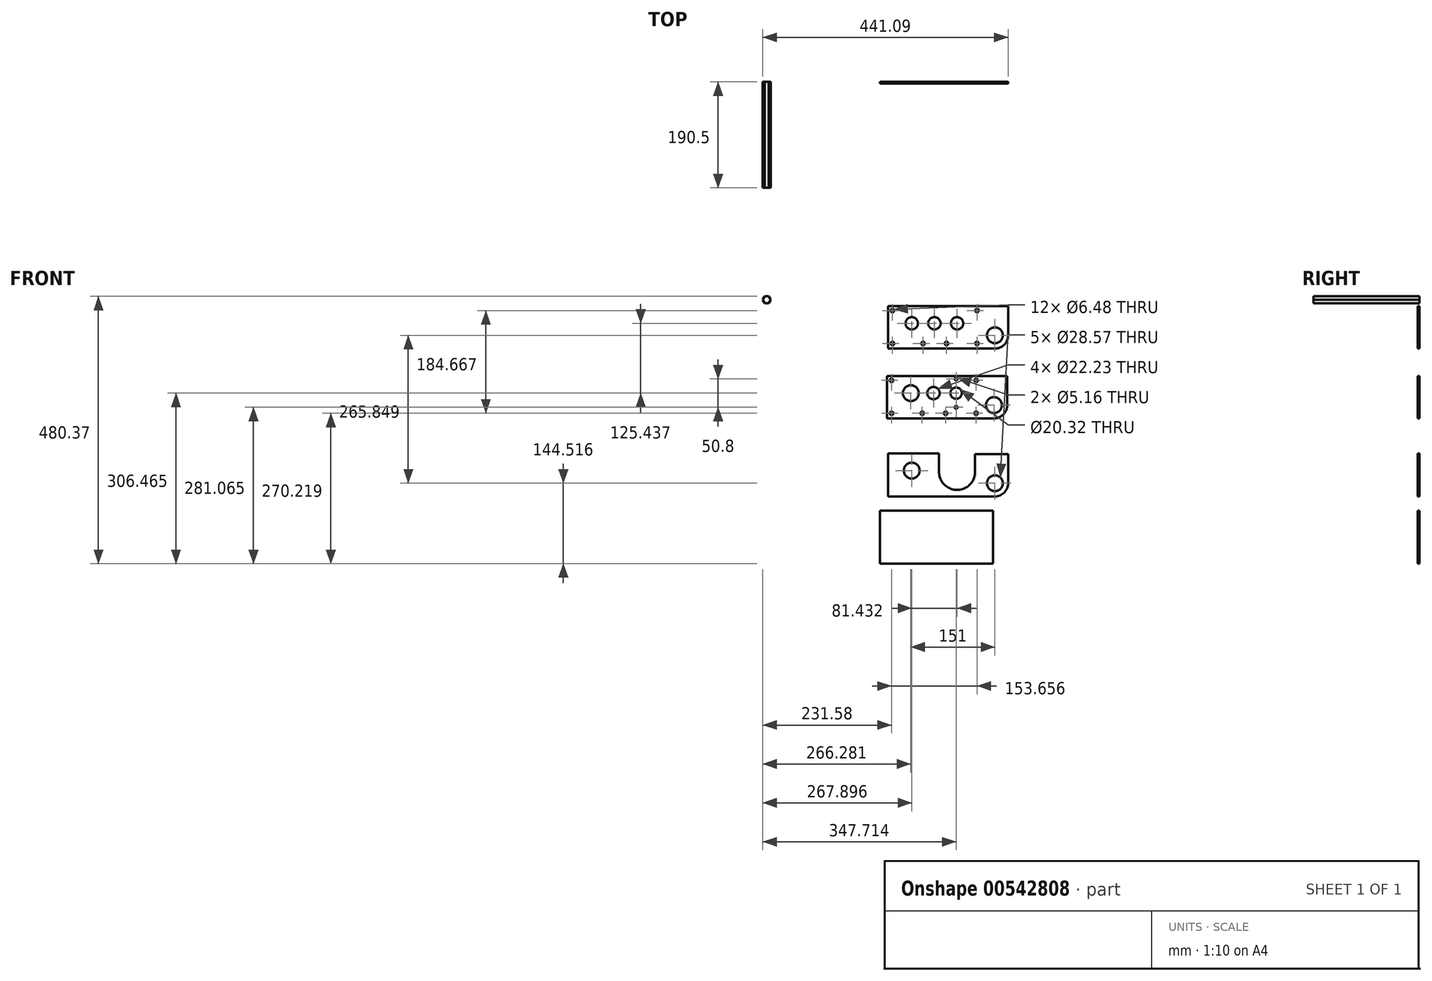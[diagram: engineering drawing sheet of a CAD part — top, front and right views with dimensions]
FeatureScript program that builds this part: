
annotation { "Feature Type Name" : "Feature", "Feature Type Description" : "" }
export const myFeature = defineFeature(function(context is Context, id is Id, definition is map)
    precondition{}
    {
        {
            var Q0;
            Q0=qCreatedBy(makeId("Front.planeOp"),FACE);
            var sketch = newSketch(context, id + "F0", { "sketchPlane" : qUnion([Q0])});
            skLineSegment(sketch, "E0.bottom", {"start": v(-27.68, -46.52) * mm, "end": v(188.15, -46.52) * mm});
            skLineSegment(sketch, "E0.top", {"start": v(-27.68, -122.72) * mm, "end": v(164.34, -122.72) * mm});
            skLineSegment(sketch, "E0.left", {"start": v(-27.68, -46.52) * mm, "end": v(-27.68, -122.72) * mm});
            skLineSegment(sketch, "E0.right", {"start": v(188.15, -46.52) * mm, "end": v(188.15, -98.27) * mm});
            skCircle(sketch, "E1", {"center": v(14.96, -77.37) * mm, "radius": 11.11 * mm});
            skCircle(sketch, "E2", {"center": v(55.67, -77.37) * mm, "radius": 11.11 * mm});
            skCircle(sketch, "E3", {"center": v(96.39, -77.37) * mm, "radius": 11.11 * mm});
            skCircle(sketch, "E4", {"center": v(-19.75, -54.38) * mm, "radius": 3.24 * mm});
            skCircle(sketch, "E5", {"center": v(-19.75, -113.61) * mm, "radius": 3.24 * mm});
            skCircle(sketch, "E6", {"center": v(132.3, -54.4) * mm, "radius": 3.24 * mm});
            skCircle(sketch, "E7", {"center": v(35.28, -113.61) * mm, "radius": 3.24 * mm});
            skCircle(sketch, "E8", {"center": v(77.37, -113.61) * mm, "radius": 3.24 * mm});
            skCircle(sketch, "E9", {"center": v(132.3, -113.61) * mm, "radius": 3.24 * mm});
            skArc(sketch, "E10", {"start": v(164.34, -122.72) * mm, "mid": v(181.4, -115.52) * mm, "end": v(188.15, -98.27) * mm});
            skPoint(sketch, "E11.orphan", {"position": v(188.15, -122.72) * mm});
            skCircle(sketch, "E12", {"center": v(164.34, -98.9) * mm, "radius": 14.29 * mm});
            skLineSegment(sketch, "E13.bottom", {"start": v(-29.3, -171.95) * mm, "end": v(186.53, -171.95) * mm});
            skLineSegment(sketch, "E13.top", {"start": v(-29.3, -248.15) * mm, "end": v(162.73, -248.15) * mm});
            skLineSegment(sketch, "E13.left", {"start": v(-29.3, -171.95) * mm, "end": v(-29.3, -248.15) * mm});
            skLineSegment(sketch, "E13.right", {"start": v(186.53, -171.95) * mm, "end": v(186.53, -223.71) * mm});
            skCircle(sketch, "E14", {"center": v(13.34, -202.8) * mm, "radius": 14.29 * mm});
            skCircle(sketch, "E15", {"center": v(54.06, -202.8) * mm, "radius": 11.11 * mm});
            skCircle(sketch, "E16", {"center": v(94.77, -202.8) * mm, "radius": 10.16 * mm});
            skCircle(sketch, "E17", {"center": v(-21.36, -179.82) * mm, "radius": 3.24 * mm});
            skCircle(sketch, "E18", {"center": v(-21.36, -239.05) * mm, "radius": 3.24 * mm});
            skCircle(sketch, "E19", {"center": v(130.68, -179.83) * mm, "radius": 3.24 * mm});
            skCircle(sketch, "E20", {"center": v(33.67, -239.05) * mm, "radius": 3.24 * mm});
            skCircle(sketch, "E21", {"center": v(75.75, -239.05) * mm, "radius": 3.24 * mm});
            skCircle(sketch, "E22", {"center": v(130.68, -239.05) * mm, "radius": 3.24 * mm});
            skArc(sketch, "E23", {"start": v(162.73, -248.15) * mm, "mid": v(179.79, -240.96) * mm, "end": v(186.53, -223.71) * mm});
            skPoint(sketch, "E24.orphan", {"position": v(186.53, -248.15) * mm});
            skCircle(sketch, "E25", {"center": v(162.73, -224.34) * mm, "radius": 14.29 * mm});
            skCircle(sketch, "E26", {"center": v(94.77, -177.4) * mm, "radius": 2.58 * mm});
            skCircle(sketch, "E27", {"center": v(94.77, -228.2) * mm, "radius": 2.58 * mm});
            skLineSegment(sketch, "E28.top", {"start": v(-27.68, -388.57) * mm, "end": v(164.33, -388.57) * mm});
            skLineSegment(sketch, "E28.left", {"start": v(-27.68, -311.16) * mm, "end": v(-27.68, -388.57) * mm});
            skLineSegment(sketch, "E28.right", {"start": v(188.15, -312.37) * mm, "end": v(188.15, -364.75) * mm});
            skCircle(sketch, "E29", {"center": v(14.96, -342.01) * mm, "radius": 14.29 * mm});
            skArc(sketch, "E30", {"start": v(164.33, -388.57) * mm, "mid": v(181.17, -381.6) * mm, "end": v(188.15, -364.75) * mm});
            skPoint(sketch, "E31.orphan", {"position": v(188.15, -388.57) * mm});
            skCircle(sketch, "E32", {"center": v(164.33, -364.75) * mm, "radius": 14.29 * mm});
            skLineSegment(sketch, "E33", {"start": v(188.15, -312.37) * mm, "end": v(128.8, -312.37) * mm});
            skLineSegment(sketch, "E34", {"start": v(-27.68, -311.16) * mm, "end": v(64.03, -311.16) * mm});
            skLineSegment(sketch, "E35", {"start": v(64.03, -311.16) * mm, "end": v(64.03, -344.38) * mm});
            skLineSegment(sketch, "E36", {"start": v(128.8, -312.37) * mm, "end": v(128.8, -342.7) * mm});
            skArc(sketch, "E37", {"start": v(64.03, -344.38) * mm, "mid": v(97.27, -376.78) * mm, "end": v(128.8, -342.7) * mm});
            skLineSegment(sketch, "E38.bottom", {"start": v(-42.12, -414.02) * mm, "end": v(161.08, -414.02) * mm});
            skLineSegment(sketch, "E38.top", {"start": v(-42.12, -509.27) * mm, "end": v(161.08, -509.27) * mm});
            skLineSegment(sketch, "E38.left", {"start": v(-42.12, -414.02) * mm, "end": v(-42.12, -509.27) * mm});
            skLineSegment(sketch, "E38.right", {"start": v(161.08, -414.02) * mm, "end": v(161.08, -509.27) * mm});
            skCircle(sketch, "E39.cCircle", {"center": v(-245.6, -35.25) * mm, "radius": 6.35 * mm, "construction": true});
            skLineSegment(sketch, "E39.0", {"start": v(-241.94, -41.6) * mm, "end": v(-249.27, -41.6) * mm});
            skLineSegment(sketch, "E39.1", {"start": v(-249.27, -41.6) * mm, "end": v(-252.94, -35.25) * mm});
            skLineSegment(sketch, "E39.2", {"start": v(-252.94, -35.25) * mm, "end": v(-249.27, -28.9) * mm});
            skLineSegment(sketch, "E39.3", {"start": v(-249.27, -28.9) * mm, "end": v(-241.94, -28.9) * mm});
            skLineSegment(sketch, "E39.4", {"start": v(-241.94, -28.9) * mm, "end": v(-238.27, -35.25) * mm});
            skLineSegment(sketch, "E39.5", {"start": v(-238.27, -35.25) * mm, "end": v(-241.94, -41.6) * mm});
            skPoint(sketch, "E39.0.midPoint", {"position": v(-245.6, -41.6) * mm});
            skPoint(sketch, "E40.orphan", {"position": v(188.15, -375.19) * mm});
            skSolve(sketch);
        }
        {
            var Q0;
            Q0=makeQuery(id+"F0.imprint","IMPRINT",FACE,{"disambiguationData":[TD([[makeQuery(id+"F0.imprint","IMPRINT",EDGE,{"derivedFrom":sQuery(id+"F0.wireOp",EDGE,"E13.bottom")}),-1.0]])]});
            var Q1;
            Q1=makeQuery(id+"F0.imprint","IMPRINT",FACE,{"disambiguationData":[TD([[makeQuery(id+"F0.imprint","IMPRINT",EDGE,{"derivedFrom":sQuery(id+"F0.wireOp",EDGE,"E38.bottom")}),-1.0]])]});
            var Q2;
            Q2=makeQuery(id+"F0.imprint","IMPRINT",FACE,{"disambiguationData":[TD([[makeQuery(id+"F0.imprint","IMPRINT",EDGE,{"derivedFrom":sQuery(id+"F0.wireOp",EDGE,"E0.bottom")}),-1.0]])]});
            var Q3;
            Q3=makeQuery(id+"F0.imprint","IMPRINT",FACE,{"disambiguationData":[TD([[makeQuery(id+"F0.imprint","IMPRINT",EDGE,{"derivedFrom":sQuery(id+"F0.wireOp",EDGE,"E28.top")}),1.0]])]});
            extrude(context, id + "F1", {"entities" : qUnion([Q0, Q1, Q2, Q3]), "depth" : 3.17 * mm, "offsetDistance" : 25.4 * mm});
        }
        {
            var Q0;
            Q0=makeQuery(id+"F0.imprint","IMPRINT",FACE,{"disambiguationData":[TD([[makeQuery(id+"F0.imprint","IMPRINT",EDGE,{"derivedFrom":sQuery(id+"F0.wireOp",EDGE,"E39.0")}),-1.0]])]});
            extrude(context, id + "F2", {"entities" : qUnion([Q0]), "depth" : 190.5 * mm});
        }
    });
